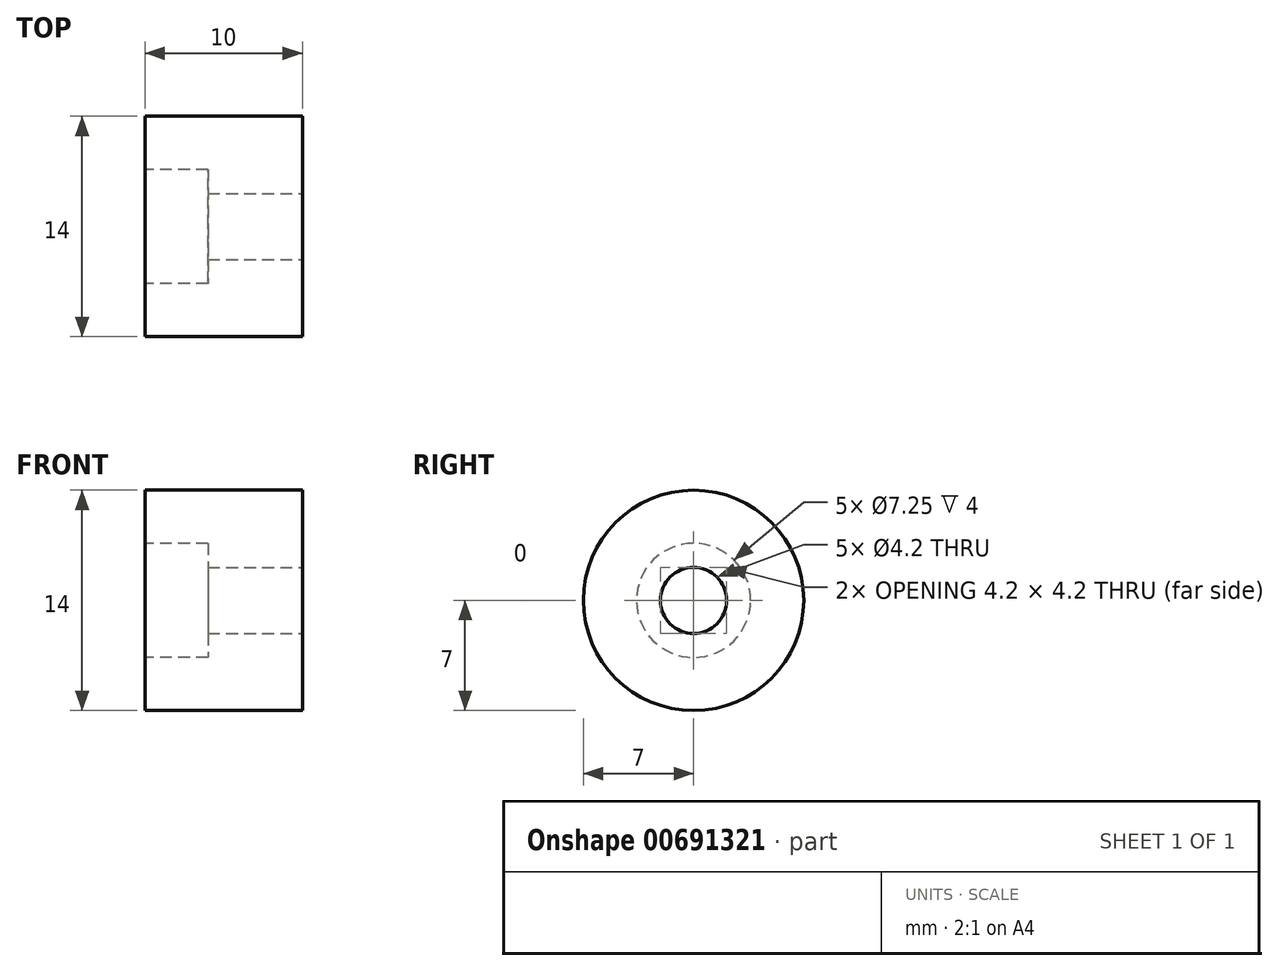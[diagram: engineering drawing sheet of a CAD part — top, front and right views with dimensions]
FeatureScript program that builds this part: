
annotation { "Feature Type Name" : "Feature", "Feature Type Description" : "" }
export const myFeature = defineFeature(function(context is Context, id is Id, definition is map)
    precondition{}
    {
        {
            var Q0;
            Q0=qCreatedBy(makeId("Right.planeOp"),FACE);
            var sketch = newSketch(context, id + "F0", { "sketchPlane" : qUnion([Q0])});
            skCircle(sketch, "E0", {"center": v(0, 0) * mm, "radius": 7 * mm});
            skSolve(sketch);
        }
        {
            var Q0;
            Q0 = qSketchRegion(id + "F0", true);
            extrude(context, id + "F1", {"entities" : qUnion([Q0]), "depth" : 10 * mm, "offsetDistance" : 25.4 * mm});
        }
        {
            var Q0;
            Q0=makeQuery(id+"F1.opExtrude","CAP_FACE",FACE,{"disambiguationData":[OSD([sQuery(id+"F0.wireOp",EDGE,"E0")])],"isStart":true});
            var sketch = newSketch(context, id + "F2", { "sketchPlane" : qUnion([Q0])});
            skCircle(sketch, "E1", {"center": v(0, 0) * mm, "radius": 3.62 * mm});
            skSolve(sketch);
        }
        {
            var Q0;
            Q0=makeQuery(id+"F2.imprint","IMPRINT",FACE,{"disambiguationData":[TD([[makeQuery(id+"F2.imprint","IMPRINT",EDGE,{"derivedFrom":sQuery(id+"F2.wireOp",EDGE,"E1")}),1.0]])]});
            var Q1;
            Q1=sQuery(id+"F2.wireOp",EDGE,"E1");
            extrude(context, id + "F3", {"entities" : qUnion([Q0]), "operationType" : NewBodyOperationType.REMOVE, "surfaceEntities" : qUnion([Q1]), "oppositeDirection" : true, "depth" : 4 * mm, "offsetDistance" : 25.4 * mm});
        }
        {
            var Q0;
            Q0=makeQuery(id+"F1.opExtrude","CAP_FACE",FACE,{"disambiguationData":[OSD([sQuery(id+"F0.wireOp",EDGE,"E0")])],"isStart":false});
            var sketch = newSketch(context, id + "F4", { "sketchPlane" : qUnion([Q0])});
            skCircle(sketch, "E2", {"center": v(0, 0) * mm, "radius": 2.1 * mm});
            skSolve(sketch);
        }
        {
            var Q0;
            Q0=makeQuery(id+"F4.imprint","IMPRINT",FACE,{"disambiguationData":[TD([[makeQuery(id+"F4.imprint","IMPRINT",EDGE,{"derivedFrom":sQuery(id+"F4.wireOp",EDGE,"E2")}),1.0]])]});
            extrude(context, id + "F5", {"entities" : qUnion([Q0]), "operationType" : NewBodyOperationType.REMOVE, "endBound" : BoundingType.THROUGH_ALL, "oppositeDirection" : true, "depth" : 25.4 * mm, "offsetDistance" : 25.4 * mm});
        }
    });
